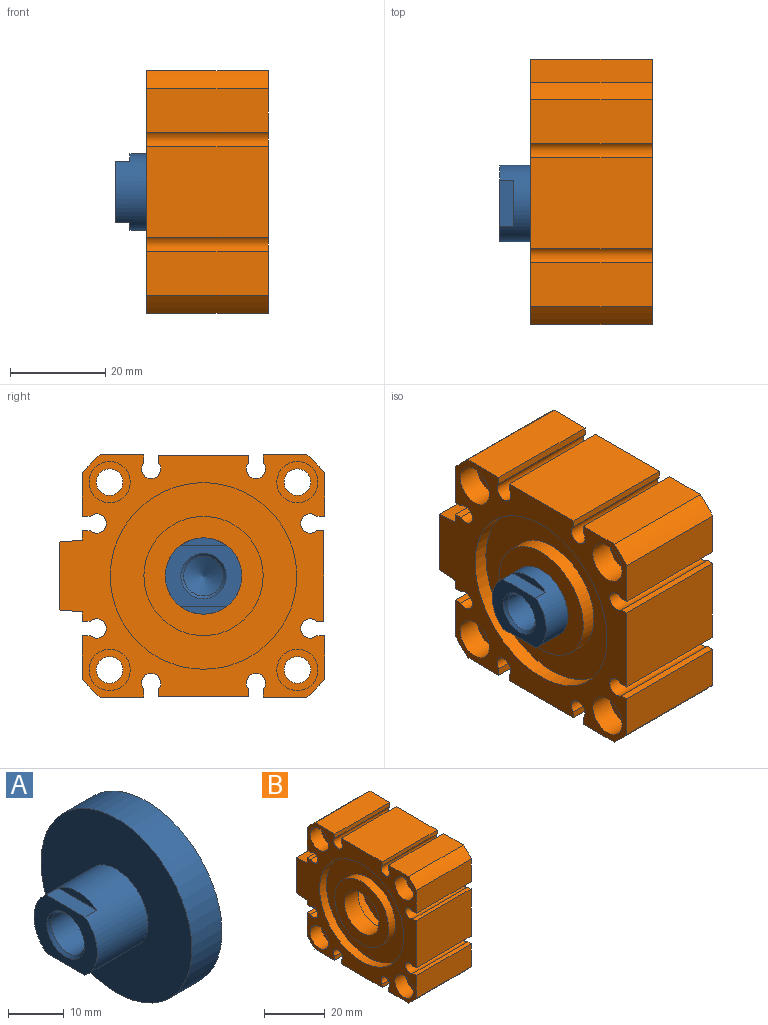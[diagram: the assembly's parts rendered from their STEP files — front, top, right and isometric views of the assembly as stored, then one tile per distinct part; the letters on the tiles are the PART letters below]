
ASSEMBLY  parts=2 mates=1
PART A: 12 faces, bbox 20.4x38.1x38.1 mm
  f0: cylinder r=19.05mm len=38.1mm, axis (1,0,0), area 912.1mm2, adj f6,f7
  f1: cylinder r=8mm len=16mm, axis (1,0,0), area 582mm2, adj f5,f6,f8,f9,f10,f11
  f2: cone r=4.19mm half-angle=45deg, axis (-1,0,0), area 22.8mm2, adj f3,f5
  f3: cylinder r=4.19mm len=12.13mm, axis (1,0,0), area 319.2mm2, adj f2,f4
  f4: cone r=1732.05mm half-angle=60deg, axis (-1,0,0), area 63.7mm2, adj f3
  f5: plane 16x12.7mm, normal (-1,0,0), area 107.9mm2, adj f1,f2,f9,f10
  f6: plane 38.1x38.1mm, normal (-1,0,0), area 939mm2, adj f0,f1
  f7: plane 38.1x38.1mm, normal (1,0,0), area 1140.1mm2, adj f0
  f8: plane 9.74x1.65mm, normal (-1,0,0), area 11mm2, adj f1,f9
  f9: plane 9.74x3mm, normal (0,0,1), area 29.2mm2, adj f1,f5,f8
  f10: plane 9.74x3mm, normal (0,0,-1), area 29.2mm2, adj f1,f5,f11
  f11: plane 9.74x1.65mm, normal (-1,0,0), area 11mm2, adj f1,f10
PART B: 77 faces, bbox 25.5x55.6x50.8 mm
  f0: cylinder r=4.32mm len=8.64mm, axis (1,0,0), area 137.8mm2, adj f63,f76
  f1: cylinder r=2.79mm len=15.37mm, axis (1,0,0), area 269.8mm2, adj f75,f76
  f2: cylinder r=4.32mm len=8.64mm, axis (1,0,0), area 137.8mm2, adj f64,f75
  f3: cylinder r=4.32mm len=8.64mm, axis (1,0,0), area 137.8mm2, adj f63,f74
  f4: cylinder r=2.79mm len=15.37mm, axis (1,0,0), area 269.8mm2, adj f73,f74
  f5: cylinder r=4.32mm len=8.64mm, axis (1,0,0), area 137.8mm2, adj f64,f73
  f6: cylinder r=4.32mm len=8.64mm, axis (1,0,0), area 137.8mm2, adj f63,f72
  f7: cylinder r=2.79mm len=15.37mm, axis (1,0,0), area 269.8mm2, adj f71,f72
  f8: cylinder r=4.32mm len=8.64mm, axis (1,0,0), area 137.8mm2, adj f64,f71
  f9: cylinder r=4.32mm len=8.64mm, axis (1,0,0), area 137.8mm2, adj f63,f70
  f10: cylinder r=2.79mm len=15.37mm, axis (1,0,0), area 269.8mm2, adj f69,f70
  f11: cylinder r=4.32mm len=8.64mm, axis (1,0,0), area 137.8mm2, adj f64,f69
  f12: cone r=4.28mm half-angle=60deg, axis (0,1,0), area 66.5mm2, adj f13
  f13: cylinder r=4.28mm len=8.57mm, axis (0,-1,0), area 151.2mm2, adj f12,f14
  f14: cone r=4.86mm half-angle=45deg, axis (0,1,0), area 23.6mm2, adj f13,f49
  f15: cylinder r=19.05mm len=38.1mm, axis (1,0,0), area 1292.1mm2, adj f67,f68
  f16: cylinder r=8mm len=16mm, axis (1,0,0), area 319.2mm2, adj f66,f67
  f17: cylinder r=19.55mm len=39.1mm, axis (-1,0,0), area 390mm2, adj f64,f65
  f18: cylinder r=12.5mm len=25mm, axis (-1,0,0), area 249.4mm2, adj f65,f66
  f19: cylinder r=2.02mm len=25.53mm, axis (-1,0,0), area 238.6mm2, adj f52,f53,f63,f64
  f20: cylinder r=2.02mm len=25.53mm, axis (-1,0,0), area 238.6mm2, adj f45,f46,f63,f64
  f21: cylinder r=2.02mm len=25.53mm, axis (-1,0,0), area 238.6mm2, adj f40,f41,f63,f64
  f22: cylinder r=2.02mm len=25.53mm, axis (-1,0,0), area 238.6mm2, adj f37,f38,f63,f64
  f23: cylinder r=2.02mm len=25.53mm, axis (-1,0,0), area 238.6mm2, adj f32,f33,f63,f64
  f24: cylinder r=2.02mm len=25.53mm, axis (-1,0,0), area 238.6mm2, adj f29,f30,f63,f64
  f25: plane 25.53x1.64mm, normal (0,1,0), area 41.9mm2, adj f26,f62,f63,f64
  f26: plane 25.53x9.19mm, normal (0,0,1), area 234.6mm2, adj f25,f27,f63,f64
  f27: cylinder r=33.4mm len=25.53mm, axis (-1,0,0), area 134.1mm2, adj f26,f28,f63,f64
  f28: plane 25.53x9.19mm, normal (0,-1,0), area 234.6mm2, adj f27,f29,f63,f64
  f29: plane 25.53x1.64mm, normal (0,0,-1), area 41.9mm2, adj f24,f28,f63,f64
  f30: plane 25.53x1.49mm, normal (0,0,1), area 38mm2, adj f24,f31,f63,f64
  f31: plane 25.53x19mm, normal (0,-1,0), area 485mm2, adj f30,f32,f63,f64
  f32: plane 25.53x1.49mm, normal (0,0,-1), area 38mm2, adj f23,f31,f63,f64
  f33: plane 25.53x1.64mm, normal (0,0,1), area 41.9mm2, adj f23,f34,f63,f64
  f34: plane 25.53x9.19mm, normal (0,-1,0), area 234.6mm2, adj f33,f35,f63,f64
  f35: cylinder r=33.4mm len=25.53mm, axis (-1,0,0), area 134.1mm2, adj f34,f36,f63,f64
  f36: plane 25.53x9.19mm, normal (0,0,-1), area 234.6mm2, adj f35,f37,f63,f64
  f37: plane 25.53x1.64mm, normal (0,1,0), area 41.9mm2, adj f22,f36,f63,f64
  f38: plane 25.53x1.49mm, normal (0,-1,0), area 38mm2, adj f22,f39,f63,f64
  f39: plane 25.53x19mm, normal (0,0,-1), area 485mm2, adj f38,f40,f63,f64
  f40: plane 25.53x1.49mm, normal (0,1,0), area 38mm2, adj f21,f39,f63,f64
  f41: plane 25.53x1.64mm, normal (0,-1,0), area 41.9mm2, adj f21,f42,f63,f64
  f42: plane 25.53x9.19mm, normal (0,0,-1), area 234.6mm2, adj f41,f43,f63,f64
  f43: cylinder r=33.4mm len=25.53mm, axis (-1,0,0), area 134.1mm2, adj f42,f44,f63,f64
  f44: plane 25.53x9.19mm, normal (0,1,0), area 234.6mm2, adj f43,f45,f63,f64
  f45: plane 25.53x1.64mm, normal (0,0,1), area 41.9mm2, adj f20,f44,f63,f64
  f46: plane 25.53x1.64mm, normal (0,0,-1), area 41.9mm2, adj f20,f47,f63,f64
  f47: plane 25.53x1.97mm, normal (0,1,0), area 50.2mm2, adj f46,f48,f63,f64
  f48: plane 25.53x4.83mm, normal (0,0.09,-1), area 123.7mm2, adj f47,f49,f63,f64
  f49: plane 25.53x14.22mm, normal (0,1,0), area 288.8mm2, adj f14,f48,f50,f63,f64
  f50: plane 25.53x4.83mm, normal (0,0.09,1), area 123.7mm2, adj f49,f51,f63,f64
  f51: plane 25.53x1.97mm, normal (0,1,0), area 50.2mm2, adj f50,f52,f63,f64
  f52: plane 25.53x1.64mm, normal (0,0,1), area 41.9mm2, adj f19,f51,f63,f64
  f53: plane 25.53x1.64mm, normal (0,0,-1), area 41.9mm2, adj f19,f54,f63,f64
  f54: plane 25.53x9.19mm, normal (0,1,0), area 234.6mm2, adj f53,f55,f63,f64
  f55: cylinder r=33.4mm len=25.53mm, axis (-1,0,0), area 134.1mm2, adj f54,f56,f63,f64
  f56: plane 25.53x9.19mm, normal (0,0,1), area 234.6mm2, adj f55,f57,f63,f64
  f57: plane 25.53x1.64mm, normal (0,-1,0), area 41.9mm2, adj f56,f58,f63,f64
  f58: cylinder r=2.02mm len=25.53mm, axis (-1,0,0), area 238.6mm2, adj f57,f59,f63,f64
  f59: plane 25.53x1.49mm, normal (0,1,0), area 38mm2, adj f58,f60,f63,f64
  f60: plane 25.53x19mm, normal (0,0,1), area 485mm2, adj f59,f61,f63,f64
  f61: plane 25.53x1.49mm, normal (0,-1,0), area 38mm2, adj f60,f62,f63,f64
  f62: cylinder r=2.02mm len=25.53mm, axis (-1,0,0), area 238.6mm2, adj f25,f61,f63,f64
  f63: plane 55.63x50.8mm, normal (1,0,0), area 2251mm2, adj f0,f3,f6,f9,f19,f20,f21,f22
  f64: plane 55.63x50.8mm, normal (-1,0,0), area 1050.3mm2, adj f2,f5,f8,f11,f17,f19,f20,f21
  f65: plane 39.1x39.1mm, normal (-1,0,0), area 709.9mm2, adj f17,f18
  f66: plane 25x25mm, normal (-1,0,0), area 289.8mm2, adj f16,f18
  f67: plane 38.1x38.1mm, normal (1,0,0), area 939mm2, adj f15,f16
  f68: plane 38.1x38.1mm, normal (-1,0,0), area 1140.1mm2, adj f15
  f69: plane 8.64x8.64mm, normal (-1,0,0), area 34.1mm2, adj f10,f11
  f70: plane 8.64x8.64mm, normal (1,0,0), area 34.1mm2, adj f9,f10
  f71: plane 8.64x8.64mm, normal (-1,0,0), area 34.1mm2, adj f7,f8
  f72: plane 8.64x8.64mm, normal (1,0,0), area 34.1mm2, adj f6,f7
  f73: plane 8.64x8.64mm, normal (-1,0,0), area 34.1mm2, adj f4,f5
  f74: plane 8.64x8.64mm, normal (1,0,0), area 34.1mm2, adj f3,f4
  f75: plane 8.64x8.64mm, normal (-1,0,0), area 34.1mm2, adj f1,f2
  f76: plane 8.64x8.64mm, normal (1,0,0), area 34.1mm2, adj f0,f1
PLACE A t=(-3.17,0,0)mm
PLACE B at identity fixed
MATE cylindrical B.f43 <-> A.f0  axis (1,0,0) through (6.35,0,0)mm
